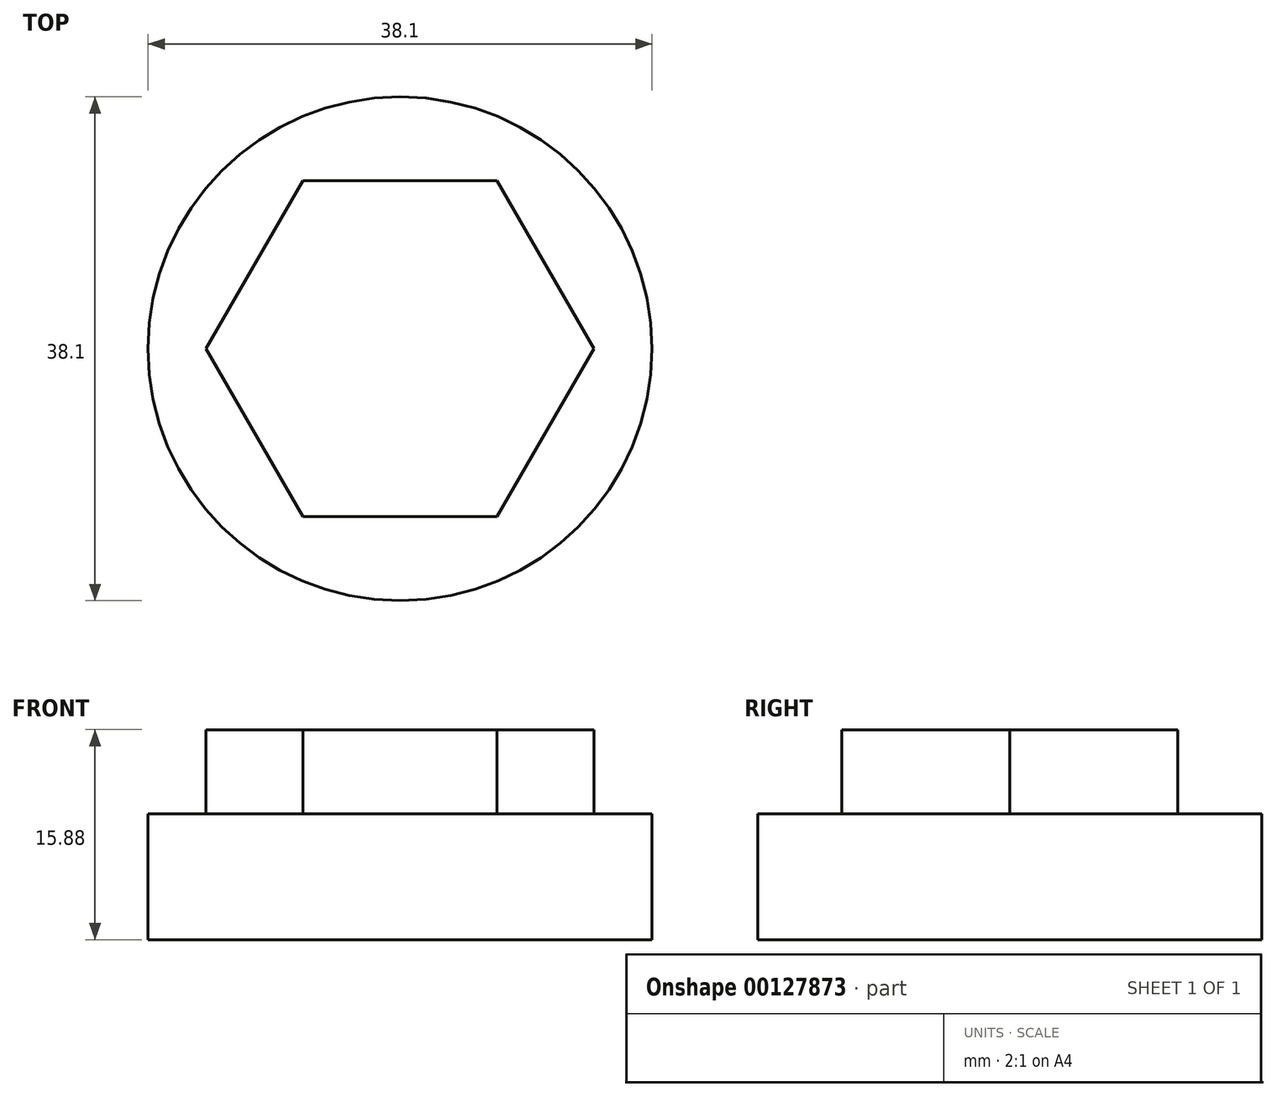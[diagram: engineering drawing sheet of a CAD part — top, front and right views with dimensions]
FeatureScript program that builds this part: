
annotation { "Feature Type Name" : "Feature", "Feature Type Description" : "" }
export const myFeature = defineFeature(function(context is Context, id is Id, definition is map)
    precondition{}
    {
        {
            var Q0;
            Q0=qCreatedBy(makeId("Top.planeOp"),FACE);
            var sketch = newSketch(context, id + "F0", { "sketchPlane" : qUnion([Q0])});
            skCircle(sketch, "E0", {"center": v(0, 0) * mm, "radius": 19.05 * mm});
            skSolve(sketch);
        }
        {
            var Q0;
            Q0=makeQuery(id+"F0.imprint","IMPRINT",FACE,{"disambiguationData":[TD([[makeQuery(id+"F0.imprint","IMPRINT",EDGE,{"derivedFrom":sQuery(id+"F0.wireOp",EDGE,"E0")}),1.0]])]});
            extrude(context, id + "F1", {"entities" : qUnion([Q0]), "depth" : 9.52 * mm});
        }
        {
            var Q0;
            Q0=makeQuery(id+"F1.opExtrude","CAP_FACE",FACE,{"disambiguationData":[OSD([sQuery(id+"F0.wireOp",EDGE,"E0")])],"isStart":false});
            var sketch = newSketch(context, id + "F2", { "sketchPlane" : qUnion([Q0])});
            skCircle(sketch, "E1.cCircle", {"center": v(0, 0) * mm, "radius": 12.7 * mm, "construction": true});
            skLineSegment(sketch, "E1.0", {"start": v(7.33, -12.7) * mm, "end": v(-7.33, -12.7) * mm});
            skLineSegment(sketch, "E1.1", {"start": v(-7.33, -12.7) * mm, "end": v(-14.66, 0) * mm});
            skLineSegment(sketch, "E1.2", {"start": v(-14.66, 0) * mm, "end": v(-7.33, 12.7) * mm});
            skLineSegment(sketch, "E1.3", {"start": v(-7.33, 12.7) * mm, "end": v(7.33, 12.7) * mm});
            skLineSegment(sketch, "E1.4", {"start": v(7.33, 12.7) * mm, "end": v(14.66, 0) * mm});
            skLineSegment(sketch, "E1.5", {"start": v(14.66, 0) * mm, "end": v(7.33, -12.7) * mm});
            skPoint(sketch, "E1.0.midPoint", {"position": v(0, -12.7) * mm});
            skSolve(sketch);
        }
        {
            var Q0;
            Q0=makeQuery(id+"F2.imprint","IMPRINT",FACE,{"disambiguationData":[TD([[makeQuery(id+"F2.imprint","IMPRINT",EDGE,{"derivedFrom":sQuery(id+"F2.wireOp",EDGE,"E1.0")}),-1.0]])]});
            extrude(context, id + "F3", {"entities" : qUnion([Q0]), "operationType" : NewBodyOperationType.ADD, "depth" : 6.35 * mm});
        }
    });
